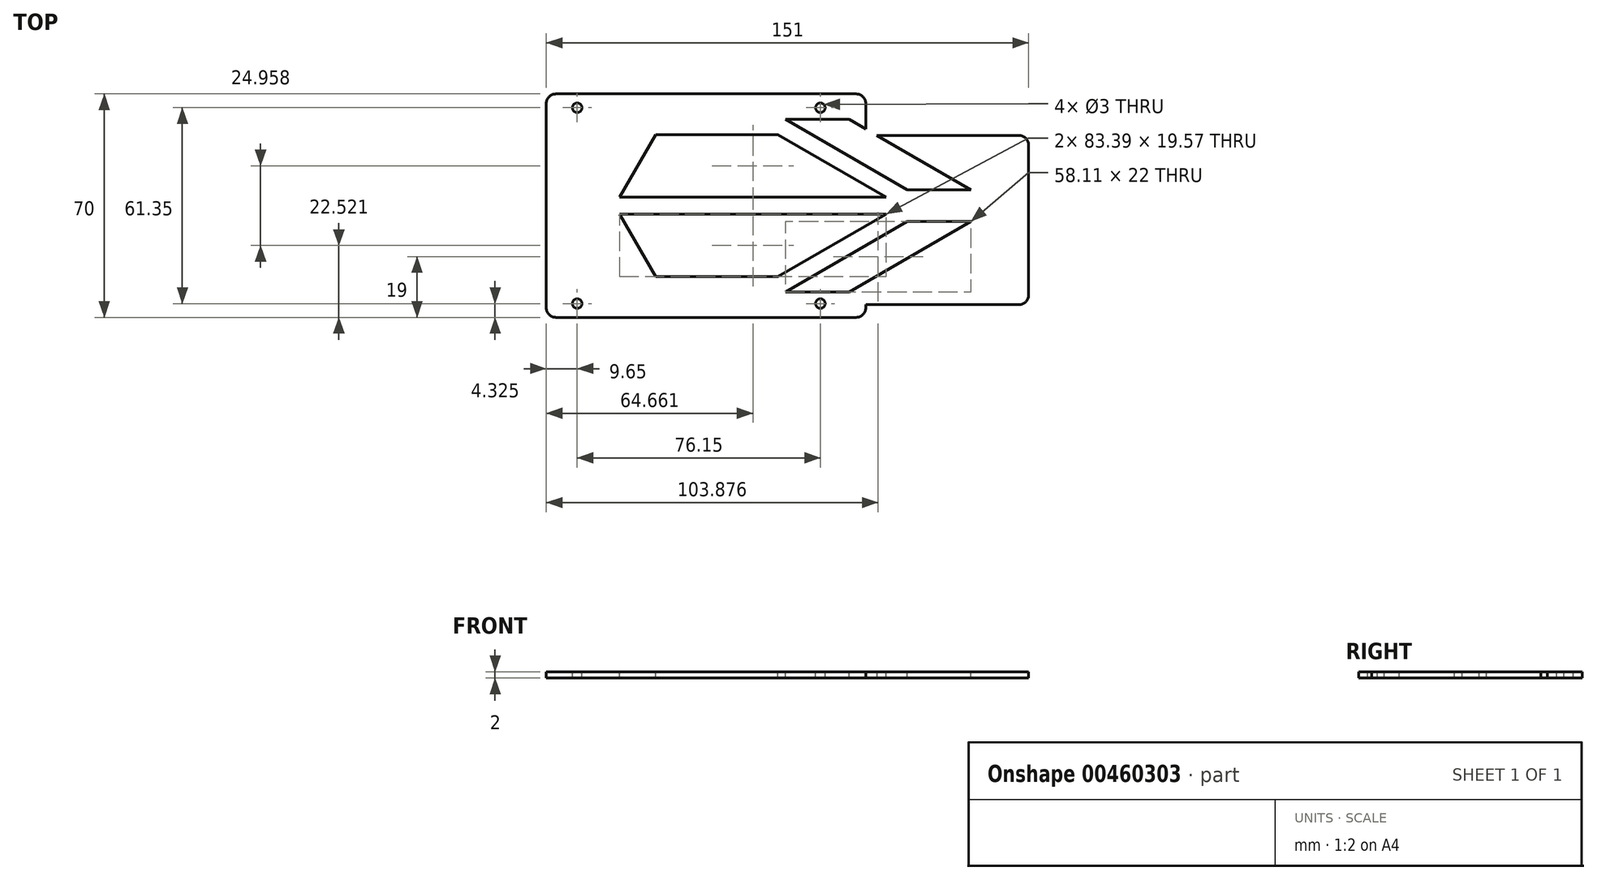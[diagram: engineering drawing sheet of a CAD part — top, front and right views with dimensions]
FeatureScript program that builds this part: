
annotation { "Feature Type Name" : "Feature", "Feature Type Description" : "" }
export const myFeature = defineFeature(function(context is Context, id is Id, definition is map)
    precondition{}
    {
        {
            var Q0;
            Q0=qCreatedBy(makeId("Top.planeOp"),FACE);
            var sketch = newSketch(context, id + "F0", { "sketchPlane" : qUnion([Q0])});
            skLineSegment(sketch, "E0.bottom", {"start": v(3, 70) * mm, "end": v(97, 70) * mm});
            skLineSegment(sketch, "E0.top", {"start": v(3, 0) * mm, "end": v(97, 0) * mm});
            skLineSegment(sketch, "E0.left", {"start": v(0, 67) * mm, "end": v(0, 3) * mm});
            skLineSegment(sketch, "E0.right", {"start": v(100, 67) * mm, "end": v(100, 57) * mm});
            skCircle(sketch, "E1", {"center": v(9.65, 65.67) * mm, "radius": 1.5 * mm});
            skCircle(sketch, "E2.MirrorC", {"center": v(85.8, 65.67) * mm, "radius": 1.5 * mm});
            skPoint(sketch, "E3.visualSharp", {"position": v(0, 70) * mm});
            skArc(sketch, "E3.filletArc", {"start": v(3, 70) * mm, "mid": v(0.88, 69.12) * mm, "end": v(0, 67) * mm});
            skPoint(sketch, "E4.visualSharp", {"position": v(0, 0) * mm});
            skArc(sketch, "E4.filletArc", {"start": v(0, 3) * mm, "mid": v(0.88, 0.88) * mm, "end": v(3, 0) * mm});
            skPoint(sketch, "E5.visualSharp", {"position": v(100, 0) * mm});
            skArc(sketch, "E5.filletArc", {"start": v(97, 0) * mm, "mid": v(99.12, 0.88) * mm, "end": v(100, 3) * mm});
            skPoint(sketch, "E6.visualSharp", {"position": v(100, 70) * mm});
            skArc(sketch, "E6.filletArc", {"start": v(100, 67) * mm, "mid": v(99.12, 69.12) * mm, "end": v(97, 70) * mm});
            skLineSegment(sketch, "E7.bottom", {"start": v(100, 57) * mm, "end": v(148, 57) * mm});
            skLineSegment(sketch, "E7.top", {"start": v(100, 4) * mm, "end": v(148, 4) * mm});
            skLineSegment(sketch, "E7.right", {"start": v(151, 54) * mm, "end": v(151, 7) * mm});
            skLineSegment(sketch, "E8", {"start": v(0, 35) * mm, "end": v(100, 35) * mm, "construction": true});
            skCircle(sketch, "E9.MirrorC", {"center": v(9.65, 4.33) * mm, "radius": 1.5 * mm});
            skCircle(sketch, "E10.MirrorC", {"center": v(85.8, 4.33) * mm, "radius": 1.5 * mm});
            skLineSegment(sketch, "E11.trimOffspring", {"start": v(100, 4) * mm, "end": v(100, 3) * mm});
            skPoint(sketch, "E12.visualSharp", {"position": v(151, 57) * mm});
            skArc(sketch, "E12.filletArc", {"start": v(151, 54) * mm, "mid": v(150.12, 56.12) * mm, "end": v(148, 57) * mm});
            skPoint(sketch, "E13.visualSharp", {"position": v(151, 4) * mm});
            skArc(sketch, "E13.filletArc", {"start": v(148, 4) * mm, "mid": v(150.12, 4.88) * mm, "end": v(151, 7) * mm});
            skSolve(sketch);
        }
        {
            var Q0;
            Q0 = qSketchRegion(id + "F0", true);
            extrude(context, id + "F1", {"entities" : qUnion([Q0]), "oppositeDirection" : true, "offsetDistance" : 25 * mm, "depth" : 2 * mm});
        }
        {
            var Q0;
            Q0=makeQuery(id+"F1.opExtrude","CAP_FACE",FACE,{"disambiguationData":[OSD([sQuery(id+"F0.wireOp",EDGE,"E0.bottom"),sQuery(id+"F0.wireOp",EDGE,"E0.top"),sQuery(id+"F0.wireOp",EDGE,"E0.left"),sQuery(id+"F0.wireOp",EDGE,"E0.right"),sQuery(id+"F0.wireOp",EDGE,"E1"),sQuery(id+"F0.wireOp",EDGE,"E2.MirrorC"),sQuery(id+"F0.wireOp",EDGE,"E3.filletArc"),sQuery(id+"F0.wireOp",EDGE,"E4.filletArc"),sQuery(id+"F0.wireOp",EDGE,"E5.filletArc"),sQuery(id+"F0.wireOp",EDGE,"E6.filletArc"),sQuery(id+"F0.wireOp",EDGE,"E7.bottom"),sQuery(id+"F0.wireOp",EDGE,"E7.top"),sQuery(id+"F0.wireOp",EDGE,"E7.right"),sQuery(id+"F0.wireOp",EDGE,"E9.MirrorC"),sQuery(id+"F0.wireOp",EDGE,"E10.MirrorC"),sQuery(id+"F0.wireOp",EDGE,"E11.trimOffspring"),sQuery(id+"F0.wireOp",EDGE,"E12.filletArc"),sQuery(id+"F0.wireOp",EDGE,"E13.filletArc")])],"isStart":false});
            var sketch = newSketch(context, id + "F2", { "sketchPlane" : qUnion([Q0])});
            skCircle(sketch, "E14", {"center": v(9.65, -65.67) * mm, "radius": 3 * mm});
            skCircle(sketch, "E15", {"center": v(85.8, -65.67) * mm, "radius": 3 * mm});
            skLineSegment(sketch, "E16", {"start": v(0, -35) * mm, "end": v(151, -35) * mm, "construction": true});
            skCircle(sketch, "E17.MirrorC", {"center": v(9.65, -4.33) * mm, "radius": 3 * mm});
            skCircle(sketch, "E18.MirrorC", {"center": v(85.8, -4.33) * mm, "radius": 3 * mm});
            skCircle(sketch, "E19", {"center": v(9.65, -65.67) * mm, "radius": 1.5 * mm});
            skCircle(sketch, "E20", {"center": v(85.8, -65.67) * mm, "radius": 1.5 * mm});
            skCircle(sketch, "E21.MirrorC", {"center": v(9.65, -4.33) * mm, "radius": 1.5 * mm});
            skCircle(sketch, "E22.MirrorC", {"center": v(85.8, -4.33) * mm, "radius": 1.5 * mm});
            skSolve(sketch);
        }
        {
            var Q0;
            Q0 = qSketchRegion(id + "F2", true);
            extrude(context, id + "F3", {"entities" : qUnion([Q0]), "operationType" : NewBodyOperationType.ADD, "oppositeDirection" : true, "offsetDistance" : 25 * mm, "depth" : 2 * mm});
        }
        {
            var Q0;
            {var subQ0=sQuery(id+"F0.wireOp",EDGE,"E5.filletArc");var subQ1=sQuery(id+"F0.wireOp",EDGE,"E4.filletArc");var subQ2=sQuery(id+"F0.wireOp",EDGE,"E3.filletArc");var subQ3=sQuery(id+"F0.wireOp",EDGE,"E2.MirrorC");var subQ4=sQuery(id+"F0.wireOp",EDGE,"E1");var subQ5=sQuery(id+"F0.wireOp",EDGE,"E6.filletArc");var subQ6=sQuery(id+"F0.wireOp",EDGE,"E0.bottom");var subQ7=sQuery(id+"F0.wireOp",EDGE,"E0.right");var subQ8=sQuery(id+"F0.wireOp",EDGE,"E0.top");var subQ9=sQuery(id+"F0.wireOp",EDGE,"E0.left");var subQ10=sQuery(id+"F0.wireOp",EDGE,"E7.bottom");var subQ11=sQuery(id+"F0.wireOp",EDGE,"E7.top");var subQ13=sQuery(id+"F0.wireOp",EDGE,"E7.right");var subQ14=sQuery(id+"F0.wireOp",EDGE,"E9.MirrorC");var subQ15=sQuery(id+"F0.wireOp",EDGE,"E10.MirrorC");var subQ16=sQuery(id+"F0.wireOp",EDGE,"E11.trimOffspring");var subQ17=sQuery(id+"F0.wireOp",EDGE,"E12.filletArc");Q0=makeQuery(id+"F4.boolean.opBoolean","SPLIT",FACE,{"disambiguationData":[TD([makeQuery(id+"F1.opExtrude","SWEPT_FACE",FACE,{"disambiguationData":[OSD([subQ6])]})])],"derivedFrom":makeQuery(id+"F1.opExtrude","CAP_FACE",FACE,{"disambiguationData":[OSD([subQ6,subQ8,subQ9,subQ7,subQ4,subQ3,subQ2,subQ1,subQ0,subQ5,subQ10,subQ11,subQ13,subQ14,subQ15,subQ16,subQ17,sQuery(id+"F0.wireOp",EDGE,"E13.filletArc")])],"isStart":false})});}
            var sketch = newSketch(context, id + "F5", { "sketchPlane" : qUnion([Q0])});
            skLineSegment(sketch, "E23", {"start": v(176.55, -35) * mm, "end": v(-18.25, -35) * mm, "construction": true});
            skLineSegment(sketch, "E24", {"start": v(151, -30.5) * mm, "end": v(67.47, -30.5) * mm, "construction": true});
            skSolve(sketch);
        }
        {
            var Q0;
            Q0=qCreatedBy(makeId("Top.planeOp"),FACE);
            var sketch = newSketch(context, id + "F6", { "sketchPlane" : qUnion([Q0])});
            skLineSegment(sketch, "E25", {"start": v(72.46, 12.74) * mm, "end": v(106.36, 32.3) * mm});
            skLineSegment(sketch, "E26", {"start": v(106.36, 32.3) * mm, "end": v(22.96, 32.3) * mm});
            skLineSegment(sketch, "E27", {"start": v(22.96, 32.3) * mm, "end": v(34.26, 12.74) * mm});
            skLineSegment(sketch, "E28", {"start": v(34.26, 12.74) * mm, "end": v(72.46, 12.74) * mm});
            skLineSegment(sketch, "E29.MirrorCS", {"start": v(72.46, 57.26) * mm, "end": v(106.36, 37.7) * mm});
            skLineSegment(sketch, "E30.MirrorCS", {"start": v(106.36, 37.7) * mm, "end": v(22.96, 37.7) * mm});
            skLineSegment(sketch, "E31.MirrorCS", {"start": v(22.96, 37.7) * mm, "end": v(34.26, 57.26) * mm});
            skLineSegment(sketch, "E32.MirrorCS", {"start": v(34.26, 57.26) * mm, "end": v(72.46, 57.26) * mm});
            skLineSegment(sketch, "E33", {"start": v(132.93, 30) * mm, "end": v(112.93, 30) * mm});
            skLineSegment(sketch, "E34", {"start": v(94.82, 8) * mm, "end": v(132.93, 30) * mm});
            skPoint(sketch, "E34.endSnap0", {"position": v(94.82, 21.44) * mm});
            skLineSegment(sketch, "E35", {"start": v(74.82, 8) * mm, "end": v(94.82, 8) * mm});
            skLineSegment(sketch, "E36", {"start": v(112.93, 30) * mm, "end": v(74.82, 8) * mm});
            skLineSegment(sketch, "E37.MirrorCS", {"start": v(132.93, 40) * mm, "end": v(112.93, 40) * mm});
            skLineSegment(sketch, "E38.MirrorCS", {"start": v(112.93, 40) * mm, "end": v(74.82, 62) * mm});
            skLineSegment(sketch, "E39.MirrorCS", {"start": v(94.82, 62) * mm, "end": v(132.93, 40) * mm});
            skLineSegment(sketch, "E40.MirrorCS", {"start": v(74.82, 62) * mm, "end": v(94.82, 62) * mm});
            skSolve(sketch);
        }
        {
            var Q0;
            Q0 = qSketchRegion(id + "F6", true);
            extrude(context, id + "F7", {"entities" : qUnion([Q0]), "operationType" : NewBodyOperationType.REMOVE, "oppositeDirection" : true, "depth" : 2 * mm, "offsetDistance" : 25 * mm});
        }
    });
